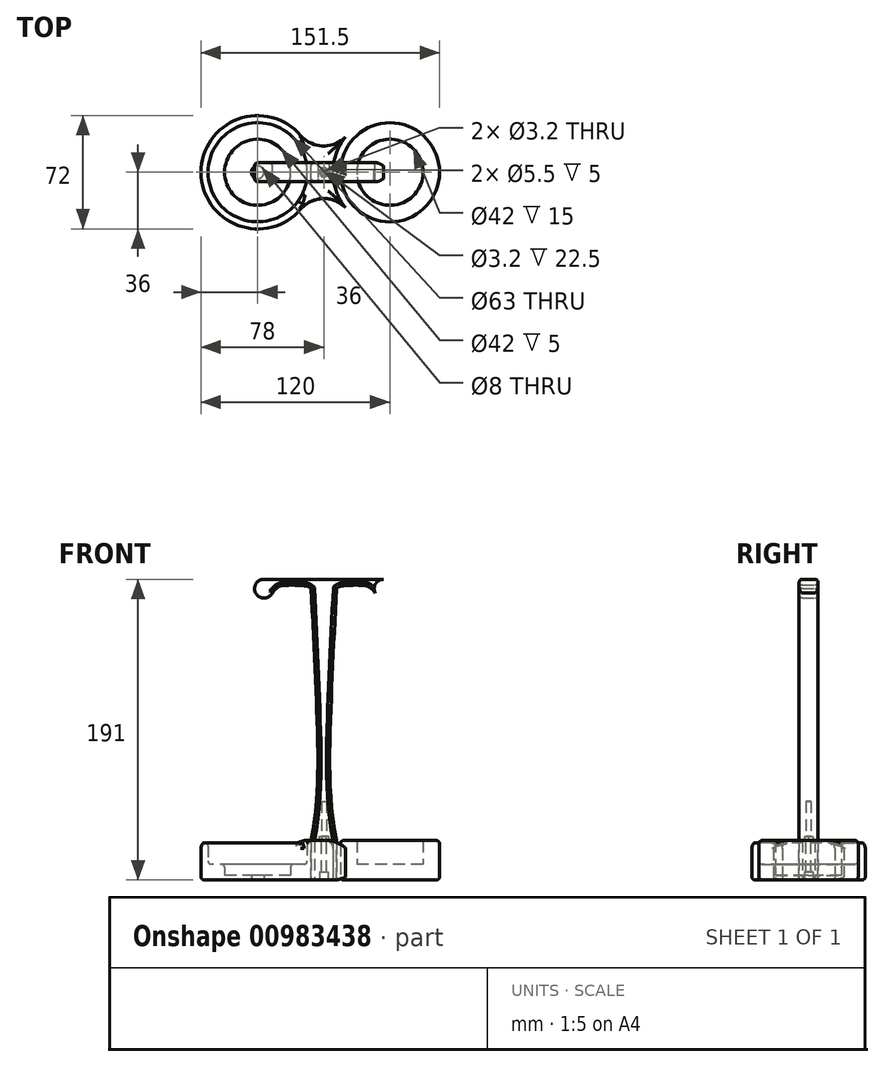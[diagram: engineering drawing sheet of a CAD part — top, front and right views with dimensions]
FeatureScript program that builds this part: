
annotation { "Feature Type Name" : "Feature", "Feature Type Description" : "" }
export const myFeature = defineFeature(function(context is Context, id is Id, definition is map)
    precondition{}
    {
        {
            var Q0;
            Q0=qCreatedBy(makeId("Top.planeOp"),FACE);
            var sketch = newSketch(context, id + "F0", { "sketchPlane" : qUnion([Q0])});
            skLineSegment(sketch, "E0", {"start": v(0, 0) * mm, "end": v(-42, 0) * mm, "construction": true});
            skCircle(sketch, "E1", {"center": v(-42, 0) * mm, "radius": 31.5 * mm});
            skCircle(sketch, "E2", {"center": v(-42, 0) * mm, "radius": 36 * mm});
            skCircle(sketch, "E3", {"center": v(-42, 0) * mm, "radius": 21 * mm});
            skCircle(sketch, "E4.MirrorC", {"center": v(41.89, 0) * mm, "radius": 36 * mm});
            skLineSegment(sketch, "E5.MirrorCS", {"start": v(0, 0) * mm, "end": v(42, 0) * mm, "construction": true});
            skLineSegment(sketch, "E6", {"start": v(0, 0) * mm, "end": v(0, 36) * mm, "construction": true});
            skLineSegment(sketch, "E7", {"start": v(0, 0) * mm, "end": v(0, -36) * mm, "construction": true});
            skArc(sketch, "E8", {"start": v(-14.67, 23.43) * mm, "mid": v(-0.74, 16.7) * mm, "end": v(13.66, 22.34) * mm});
            skArc(sketch, "E9.MirrorC", {"start": v(-14.67, -23.43) * mm, "mid": v(-0.74, -16.7) * mm, "end": v(13.66, -22.34) * mm});
            skCircle(sketch, "E10.MirrorC", {"center": v(42, 0) * mm, "radius": 21 * mm});
            skCircle(sketch, "E11.MirrorC", {"center": v(42, 0) * mm, "radius": 31.5 * mm});
            skSolve(sketch);
        }
        {
            var Q0;
            Q0=makeQuery(id+"F0.imprint","IMPRINT",FACE,{"disambiguationData":[TD([[makeQuery(id+"F0.imprint","IMPRINT",EDGE,{"derivedFrom":sQuery(id+"F0.wireOp",EDGE,"E1")}),-1.0]])]});
            var Q1;
            {var subQ0=sQuery(id+"F0.wireOp",EDGE,"E8");Q1=makeQuery(id+"F0.imprint","IMPRINT",FACE,{"disambiguationData":[TD([[makeQuery(id+"F0.imprint","IMPRINT",EDGE,{"derivedFrom":subQ0}),-1.0]])]});}
            var Q2;
            Q2=makeQuery(id+"F0.imprint","IMPRINT",FACE,{"disambiguationData":[TD([[makeQuery(id+"F0.imprint","IMPRINT",EDGE,{"derivedFrom":sQuery(id+"F0.wireOp",EDGE,"E11.MirrorC")}),1.0]])]});
            extrude(context, id + "F1", {"entities" : qUnion([Q0, Q1, Q2]), "depth" : 25 * mm, "offsetDistance" : 25 * mm});
        }
        {
            var Q0;
            Q0=makeQuery(id+"F0.imprint","IMPRINT",FACE,{"disambiguationData":[TD([[makeQuery(id+"F0.imprint","IMPRINT",EDGE,{"derivedFrom":sQuery(id+"F0.wireOp",EDGE,"E1")}),1.0]])]});
            var Q1;
            Q1=makeQuery(id+"F0.imprint","IMPRINT",FACE,{"disambiguationData":[TD([[makeQuery(id+"F0.imprint","IMPRINT",EDGE,{"derivedFrom":sQuery(id+"F0.wireOp",EDGE,"E10.MirrorC")}),1.0]])]});
            extrude(context, id + "F2", {"entities" : qUnion([Q0, Q1]), "operationType" : NewBodyOperationType.ADD, "depth" : 10 * mm, "offsetDistance" : 25 * mm});
        }
        {
            var Q0;
            Q0=makeQuery(id+"F0.imprint","IMPRINT",FACE,{"disambiguationData":[TD([[makeQuery(id+"F0.imprint","IMPRINT",EDGE,{"derivedFrom":sQuery(id+"F0.wireOp",EDGE,"E3")}),1.0]])]});
            var Q1;
            Q1=makeQuery(id+"F0.imprint","IMPRINT",FACE,{"disambiguationData":[TD([[makeQuery(id+"F0.imprint","IMPRINT",EDGE,{"derivedFrom":sQuery(id+"F0.wireOp",EDGE,"E10.MirrorC")}),-1.0]])]});
            extrude(context, id + "F3", {"entities" : qUnion([Q0, Q1]), "operationType" : NewBodyOperationType.ADD, "depth" : 3 * mm, "offsetDistance" : 25 * mm});
        }
        {
            var Q0;
            Q0=makeQuery(id+"F1.opExtrude","CAP_EDGE",EDGE,{"disambiguationData":[OSD([sQuery(id+"F0.wireOp",EDGE,"E2")])],"isStart":false});
            var Q1;
            Q1=makeQuery(id+"F1.opExtrude","CAP_EDGE",EDGE,{"disambiguationData":[OSD([sQuery(id+"F0.wireOp",EDGE,"E4.MirrorC")])],"isStart":false});
            fillet(context, id + "F4", {"entities" : qUnion([Q0, Q1]), "radius" : 5 * mm, "tangentPropagation" : true, "allowEdgeOverflow" : false});
        }
        {
            var Q0;
            Q0=makeQuery(id+"F2.opExtrude","CAP_EDGE",EDGE,{"disambiguationData":[OSD([sQuery(id+"F0.wireOp",EDGE,"E1")])],"isStart":false});
            var Q1;
            Q1=makeQuery(id+"F2.opExtrude","CAP_EDGE",EDGE,{"disambiguationData":[OSD([sQuery(id+"F0.wireOp",EDGE,"E11.MirrorC")])],"isStart":false});
            var Q2;
            Q2=makeQuery(id+"F3.opExtrude","CAP_EDGE",EDGE,{"disambiguationData":[OSD([sQuery(id+"F0.wireOp",EDGE,"E3")])],"isStart":false});
            var Q3;
            Q3=makeQuery(id+"F3.opExtrude","CAP_EDGE",EDGE,{"disambiguationData":[OSD([sQuery(id+"F0.wireOp",EDGE,"E10.MirrorC")])],"isStart":false});
            var Q4;
            Q4=makeQuery(id+"F2.opExtrude","CAP_EDGE",EDGE,{"disambiguationData":[OSD([sQuery(id+"F0.wireOp",EDGE,"E3")])],"isStart":false});
            var Q5;
            Q5=makeQuery(id+"F2.opExtrude","CAP_EDGE",EDGE,{"disambiguationData":[OSD([sQuery(id+"F0.wireOp",EDGE,"E10.MirrorC")])],"isStart":false});
            var Q6;
            Q6=makeQuery(id+"F1.opExtrude","SWEPT_FACE",FACE,{"disambiguationData":[OSD([sQuery(id+"F0.wireOp",EDGE,"E1")])]});
            var Q7;
            Q7=makeQuery(id+"F1.opExtrude","SWEPT_FACE",FACE,{"disambiguationData":[OSD([sQuery(id+"F0.wireOp",EDGE,"E11.MirrorC")])]});
            fillet(context, id + "F5", {"entities" : qUnion([Q0, Q1, Q2, Q3, Q4, Q5, Q6, Q7]), "radius" : 2 * mm, "tangentPropagation" : true, "allowEdgeOverflow" : false});
        }
        {
            var Q0;
            {var subQ0=sQuery(id+"F0.wireOp",EDGE,"E10.MirrorC");var subQ1=sQuery(id+"F0.wireOp",EDGE,"E3");var subQ2=sQuery(id+"F0.wireOp",EDGE,"E11.MirrorC");var subQ3=sQuery(id+"F0.wireOp",EDGE,"E1");Q0=makeQuery(id+"F3.boolean.opBoolean","MERGE",FACE,{"derivedFrom":[makeQuery(id+"F2.boolean.opBoolean","MERGE",FACE,{"derivedFrom":[makeQuery(id+"F1.opExtrude","CAP_FACE",FACE,{"disambiguationData":[OSD([subQ3,sQuery(id+"F0.wireOp",EDGE,"E2"),sQuery(id+"F0.wireOp",EDGE,"E4.MirrorC"),sQuery(id+"F0.wireOp",EDGE,"E8"),sQuery(id+"F0.wireOp",EDGE,"E9.MirrorC"),subQ2])],"isStart":true}),makeQuery(id+"F2.opExtrude","CAP_FACE",FACE,{"disambiguationData":[OSD([subQ3,subQ1])],"isStart":true}),makeQuery(id+"F2.opExtrude","CAP_FACE",FACE,{"disambiguationData":[OSD([subQ0,subQ2])],"isStart":true})]}),makeQuery(id+"F3.opExtrude","CAP_FACE",FACE,{"disambiguationData":[OSD([subQ1])],"isStart":true}),makeQuery(id+"F3.opExtrude","CAP_FACE",FACE,{"disambiguationData":[OSD([subQ0])],"isStart":true})]});}
            fillet(context, id + "F6", {"entities" : qUnion([Q0]), "radius" : 2 * mm, "tangentPropagation" : true, "allowEdgeOverflow" : false});
        }
        {
            var Q0;
            Q0=qCreatedBy(makeId("Front.planeOp"),FACE);
            var sketch = newSketch(context, id + "F7", { "sketchPlane" : qUnion([Q0])});
            skLineSegment(sketch, "E12", {"start": v(0, 0) * mm, "end": v(0, 25) * mm, "construction": true});
            skLineSegment(sketch, "E13", {"start": v(0, 25) * mm, "end": v(0, 105) * mm, "construction": true});
            skLineSegment(sketch, "E14", {"start": v(0, 105) * mm, "end": v(0, 185) * mm, "construction": true});
            skFitSpline(sketch, "E15", {"points": [v(-8, 25) * mm, v(-4.38, 105) * mm, v(-8, 185) * mm], "startDerivative": vector(30.45, 149.9) * mm, "endDerivative": vector(-7.2, 152.41) * mm});
            skFitSpline(sketch, "E16.MirrorCS", {"points": [v(8, 25) * mm, v(4.38, 105) * mm, v(8, 185) * mm], "startDerivative": vector(-30.45, 149.9) * mm, "endDerivative": vector(7.2, 152.41) * mm});
            skLineSegment(sketch, "E17", {"start": v(-8, 185) * mm, "end": v(8, 185) * mm});
            skLineSegment(sketch, "E18", {"start": v(-8, 25) * mm, "end": v(8, 25) * mm});
            skLineSegment(sketch, "E19", {"start": v(-8, 185) * mm, "end": v(-38, 185) * mm, "construction": true});
            skCircle(sketch, "E20", {"center": v(-38, 185) * mm, "radius": 6 * mm});
            skLineSegment(sketch, "E21", {"start": v(-38, 191) * mm, "end": v(0, 191) * mm});
            skFitSpline(sketch, "E22", {"points": [v(-32.63, 182.33) * mm, v(-25.28, 187.05) * mm, v(-14.42, 187.05) * mm, v(-8, 185) * mm], "startDerivative": vector(28.5, 36.35) * mm, "endDerivative": vector(15.62, -16.58) * mm});
            skLineSegment(sketch, "E23.MirrorCS", {"start": v(38, 191) * mm, "end": v(0, 191) * mm});
            skFitSpline(sketch, "E24.MirrorCS", {"points": [v(32.63, 182.33) * mm, v(25.28, 187.05) * mm, v(14.42, 187.05) * mm, v(8, 185) * mm], "startDerivative": vector(-28.5, 36.35) * mm, "endDerivative": vector(-15.62, -16.58) * mm});
            skCircle(sketch, "E25.MirrorC", {"center": v(38, 185) * mm, "radius": 6 * mm});
            skSolve(sketch);
        }
        {
            var Q0;
            Q0=makeQuery(id+"F7.imprint","IMPRINT",FACE,{"disambiguationData":[TD([[makeQuery(id+"F7.imprint","IMPRINT",EDGE,{"derivedFrom":sQuery(id+"F7.wireOp",EDGE,"E15")}),-1.0]])]});
            var Q1;
            Q1=makeQuery(id+"F7.imprint","IMPRINT",FACE,{"disambiguationData":[TD([[makeQuery(id+"F7.imprint","IMPRINT",EDGE,{"derivedFrom":sQuery(id+"F7.wireOp",EDGE,"E17")}),1.0]])]});
            var Q2;
            {var subQ0=sQuery(id+"F7.wireOp",EDGE,"E20");var subQ1=makeQuery(id+"F7.imprint","INTERSECT",VERTEX,{"derivedFrom":[subQ0,sQuery(id+"F7.wireOp",EDGE,"E21")]});Q2=makeQuery(id+"F7.imprint","IMPRINT",FACE,{"disambiguationData":[TD([[makeQuery(id+"F7.imprint","IMPRINT",EDGE,{"disambiguationData":[TD([[subQ1,-1.0]])],"derivedFrom":subQ0}),1.0]])]});}
            var Q3;
            {var subQ0=sQuery(id+"F7.wireOp",EDGE,"E25.MirrorC");var subQ1=makeQuery(id+"F7.imprint","INTERSECT",VERTEX,{"derivedFrom":[sQuery(id+"F7.wireOp",EDGE,"E23.MirrorCS"),subQ0]});Q3=makeQuery(id+"F7.imprint","IMPRINT",FACE,{"disambiguationData":[TD([[makeQuery(id+"F7.imprint","IMPRINT",EDGE,{"disambiguationData":[TD([[subQ1,-1.0]])],"derivedFrom":subQ0}),-1.0]])]});}
            extrude(context, id + "F8", {"entities" : qUnion([Q0, Q1, Q2, Q3]), "endBound" : BoundingType.SYMMETRIC, "depth" : 12 * mm, "offsetDistance" : 25 * mm});
        }
        {
            var Q0;
            Q0=makeQuery(id+"F8.opExtrude","CAP_EDGE",EDGE,{"disambiguationData":[OSD([sQuery(id+"F7.wireOp",EDGE,"E15")])],"isStart":false});
            var Q1;
            Q1=makeQuery(id+"F8.opExtrude","CAP_EDGE",EDGE,{"disambiguationData":[OSD([sQuery(id+"F7.wireOp",EDGE,"E16.MirrorCS")])],"isStart":false});
            var Q2;
            Q2=makeQuery(id+"F8.opExtrude","CAP_EDGE",EDGE,{"disambiguationData":[OSD([sQuery(id+"F7.wireOp",EDGE,"E16.MirrorCS")])],"isStart":true});
            var Q3;
            Q3=makeQuery(id+"F8.opExtrude","CAP_EDGE",EDGE,{"disambiguationData":[OSD([sQuery(id+"F7.wireOp",EDGE,"E15")])],"isStart":true});
            var Q4;
            Q4=makeQuery(id+"F8.opExtrude","CAP_EDGE",EDGE,{"disambiguationData":[OSD([sQuery(id+"F7.wireOp",EDGE,"E24.MirrorCS")])],"isStart":true});
            var Q5;
            Q5=makeQuery(id+"F8.opExtrude","CAP_EDGE",EDGE,{"disambiguationData":[OSD([sQuery(id+"F7.wireOp",EDGE,"E22")])],"isStart":true});
            var Q6;
            Q6=makeQuery(id+"F8.opExtrude","CAP_EDGE",EDGE,{"disambiguationData":[OSD([sQuery(id+"F7.wireOp",EDGE,"E24.MirrorCS")])],"isStart":false});
            var Q7;
            Q7=makeQuery(id+"F8.opExtrude","CAP_EDGE",EDGE,{"disambiguationData":[OSD([sQuery(id+"F7.wireOp",EDGE,"E22")])],"isStart":false});
            var Q8;
            Q8=makeQuery(id+"F8.opExtrude","CAP_EDGE",EDGE,{"disambiguationData":[OSD([sQuery(id+"F7.wireOp",EDGE,"E20")])],"isStart":false});
            var Q9;
            Q9=makeQuery(id+"F8.opExtrude","CAP_EDGE",EDGE,{"disambiguationData":[OSD([sQuery(id+"F7.wireOp",EDGE,"E20")])],"isStart":true});
            fillet(context, id + "F9", {"entities" : qUnion([Q0, Q1, Q2, Q3, Q4, Q5, Q6, Q7, Q8, Q9]), "radius" : 2 * mm, "tangentPropagation" : true, "allowEdgeOverflow" : false});
        }
        {
            var Q0;
            Q0=sQuery(id+"F0.wireOp",VERTEX,"E0.end");
            var Q1;
            Q1=sQuery(id+"F0.wireOp",VERTEX,"E10.MirrorC.center");
            var Q2;
            Q2=makeQuery(id+"F1.opExtrude","SWEPT_BODY",BODY,{"disambiguationData":[OSD([sQuery(id+"F0.wireOp",EDGE,"E1"),sQuery(id+"F0.wireOp",EDGE,"E2"),sQuery(id+"F0.wireOp",EDGE,"E4.MirrorC"),sQuery(id+"F0.wireOp",EDGE,"E8"),sQuery(id+"F0.wireOp",EDGE,"E9.MirrorC"),sQuery(id+"F0.wireOp",EDGE,"E11.MirrorC")])]});
            hole(context, id + "F10", {"style" : HoleStyle.SIMPLE, "endStyle" : HoleEndStyle.BLIND, "oppositeDirection" : true, "holeDiameter" : 8 * mm, "majorDiameter" : 5 * mm, "holeDepth" : 6 * mm, "isTappedThrough" : true, "tappedDepth" : 12 * mm, "tapClearance" : 3, "startFromSketch" : true, "locations" : qUnion([Q0, Q1]), "scope" : qUnion([Q2])});
        }
        {
            var Q0;
            Q0=makeQuery(id+"F8.opExtrude","SWEPT_FACE",FACE,{"disambiguationData":[OSD([sQuery(id+"F7.wireOp",EDGE,"E18")])]});
            var sketch = newSketch(context, id + "F11", { "sketchPlane" : qUnion([Q0])});
            skCircle(sketch, "E26.cCircle", {"center": v(0, 0) * mm, "radius": 2.7 * mm, "construction": true});
            skLineSegment(sketch, "E26.0", {"start": v(1.56, -2.7) * mm, "end": v(-1.56, -2.7) * mm});
            skLineSegment(sketch, "E26.1", {"start": v(-1.56, -2.7) * mm, "end": v(-3.12, 0) * mm});
            skLineSegment(sketch, "E26.2", {"start": v(-3.12, 0) * mm, "end": v(-1.56, 2.7) * mm});
            skLineSegment(sketch, "E26.3", {"start": v(-1.56, 2.7) * mm, "end": v(1.56, 2.7) * mm});
            skLineSegment(sketch, "E26.4", {"start": v(1.56, 2.7) * mm, "end": v(3.12, 0) * mm});
            skLineSegment(sketch, "E26.5", {"start": v(3.12, 0) * mm, "end": v(1.56, -2.7) * mm});
            skPoint(sketch, "E26.0.midPoint", {"position": v(0, -2.7) * mm});
            skCircle(sketch, "E27", {"center": v(0, 0) * mm, "radius": 1.6 * mm});
            skSolve(sketch);
        }
        {
            var Q0;
            Q0=makeQuery(id+"F11.imprint","IMPRINT",FACE,{"disambiguationData":[TD([[makeQuery(id+"F11.imprint","IMPRINT",EDGE,{"derivedFrom":sQuery(id+"F11.wireOp",EDGE,"E26.0")}),-1.0]])]});
            extrude(context, id + "F12", {"entities" : qUnion([Q0]), "operationType" : NewBodyOperationType.REMOVE, "oppositeDirection" : true, "depth" : 2.5 * mm, "offsetDistance" : 25 * mm});
        }
        {
            var Q0;
            Q0=makeQuery(id+"F11.imprint","IMPRINT",FACE,{"disambiguationData":[TD([[makeQuery(id+"F11.imprint","IMPRINT",EDGE,{"derivedFrom":sQuery(id+"F11.wireOp",EDGE,"E27")}),1.0]])]});
            extrude(context, id + "F13", {"entities" : qUnion([Q0]), "operationType" : NewBodyOperationType.REMOVE, "oppositeDirection" : true, "depth" : 25 * mm, "offsetDistance" : 25 * mm});
        }
        {
            var Q0;
            Q0=qCreatedBy(makeId("Top.planeOp"),FACE);
            var sketch = newSketch(context, id + "F14", { "sketchPlane" : qUnion([Q0])});
            skFitSpline(sketch, "E28.0.0", {"points": [v(-5.96, -6) * mm, v(-6.1, -6) * mm, v(-6.35, -5.98) * mm, v(-6.74, -5.86) * mm, v(-7.1, -5.68) * mm, v(-7.4, -5.43) * mm, v(-7.66, -5.13) * mm, v(-7.85, -4.78) * mm, v(-7.97, -4.4) * mm, v(-8, -4.13) * mm, v(-8, -4) * mm]});
            skLineSegment(sketch, "E28.0.1", {"start": v(-8, -4) * mm, "end": v(-8, 4) * mm});
            skFitSpline(sketch, "E28.0.2", {"points": [v(-8, 4) * mm, v(-8, 4.13) * mm, v(-7.97, 4.4) * mm, v(-7.85, 4.78) * mm, v(-7.66, 5.12) * mm, v(-7.4, 5.43) * mm, v(-7.1, 5.68) * mm, v(-6.62, 5.92) * mm, v(-6.23, 6) * mm, v(-5.96, 6) * mm]});
            skLineSegment(sketch, "E28.0.3", {"start": v(-5.96, 6) * mm, "end": v(5.96, 6) * mm});
            skFitSpline(sketch, "E28.0.4", {"points": [v(5.96, 6) * mm, v(6.1, 6) * mm, v(6.35, 5.98) * mm, v(6.74, 5.86) * mm, v(7.1, 5.68) * mm, v(7.4, 5.43) * mm, v(7.66, 5.13) * mm, v(7.85, 4.78) * mm, v(7.97, 4.4) * mm, v(8, 4.13) * mm, v(8, 4) * mm]});
            skLineSegment(sketch, "E28.0.5", {"start": v(8, 4) * mm, "end": v(8, -4) * mm});
            skFitSpline(sketch, "E28.0.6", {"points": [v(8, -4) * mm, v(8, -4.13) * mm, v(7.97, -4.4) * mm, v(7.85, -4.78) * mm, v(7.66, -5.12) * mm, v(7.4, -5.43) * mm, v(7.1, -5.68) * mm, v(6.62, -5.92) * mm, v(6.23, -6) * mm, v(5.96, -6) * mm]});
            skLineSegment(sketch, "E28.0.7", {"start": v(5.96, -6) * mm, "end": v(-5.96, -6) * mm});
            skSolve(sketch);
        }
        {
            var Q0;
            Q0=makeQuery(id+"F14.imprint","IMPRINT",FACE,{"disambiguationData":[TD([[makeQuery(id+"F14.imprint","IMPRINT",EDGE,{"derivedFrom":sQuery(id+"F14.wireOp",EDGE,"E28.0.0")}),-1.0]])]});
            extrude(context, id + "F15", {"entities" : qUnion([Q0]), "depth" : 25 * mm, "offsetDistance" : 25 * mm});
        }
        {
            var Q0;
            Q0=makeQuery(id+"F11.imprint","IMPRINT",FACE,{"disambiguationData":[TD([[makeQuery(id+"F11.imprint","IMPRINT",EDGE,{"derivedFrom":sQuery(id+"F11.wireOp",EDGE,"E27")}),1.0]])]});
            extrude(context, id + "F16", {"entities" : qUnion([Q0]), "operationType" : NewBodyOperationType.REMOVE, "depth" : 25 * mm, "offsetDistance" : 25 * mm});
        }
        {
            var Q0;
            Q0=makeQuery(id+"F11.imprint","IMPRINT",FACE,{"disambiguationData":[TD([[makeQuery(id+"F11.imprint","IMPRINT",EDGE,{"derivedFrom":sQuery(id+"F11.wireOp",EDGE,"E27")}),1.0]])]});
            extrude(context, id + "F17", {"entities" : qUnion([Q0]), "operationType" : NewBodyOperationType.REMOVE, "depth" : 25 * mm, "offsetDistance" : 25 * mm});
        }
        {
            var Q0;
            {var subQ0=sQuery(id+"F0.wireOp",EDGE,"E10.MirrorC");var subQ1=sQuery(id+"F0.wireOp",EDGE,"E3");var subQ2=sQuery(id+"F0.wireOp",EDGE,"E11.MirrorC");var subQ3=sQuery(id+"F0.wireOp",EDGE,"E1");Q0=makeQuery(id+"F3.boolean.opBoolean","MERGE",FACE,{"derivedFrom":[makeQuery(id+"F2.boolean.opBoolean","MERGE",FACE,{"derivedFrom":[makeQuery(id+"F1.opExtrude","CAP_FACE",FACE,{"disambiguationData":[OSD([subQ3,sQuery(id+"F0.wireOp",EDGE,"E2"),sQuery(id+"F0.wireOp",EDGE,"E4.MirrorC"),sQuery(id+"F0.wireOp",EDGE,"E8"),sQuery(id+"F0.wireOp",EDGE,"E9.MirrorC"),subQ2])],"isStart":true}),makeQuery(id+"F2.opExtrude","CAP_FACE",FACE,{"disambiguationData":[OSD([subQ3,subQ1])],"isStart":true}),makeQuery(id+"F2.opExtrude","CAP_FACE",FACE,{"disambiguationData":[OSD([subQ0,subQ2])],"isStart":true})]}),makeQuery(id+"F3.opExtrude","CAP_FACE",FACE,{"disambiguationData":[OSD([subQ1])],"isStart":true}),makeQuery(id+"F3.opExtrude","CAP_FACE",FACE,{"disambiguationData":[OSD([subQ0])],"isStart":true})]});}
            var sketch = newSketch(context, id + "F18", { "sketchPlane" : qUnion([Q0])});
            skCircle(sketch, "E29", {"center": v(0, 0) * mm, "radius": 2.75 * mm});
            skSolve(sketch);
        }
        {
            var Q0;
            Q0=makeQuery(id+"F18.imprint","IMPRINT",FACE,{"disambiguationData":[TD([[makeQuery(id+"F18.imprint","IMPRINT",EDGE,{"derivedFrom":sQuery(id+"F18.wireOp",EDGE,"E29")}),1.0]])]});
            extrude(context, id + "F19", {"entities" : qUnion([Q0]), "operationType" : NewBodyOperationType.REMOVE, "oppositeDirection" : true, "depth" : 5 * mm, "offsetDistance" : 25 * mm});
        }
    });
